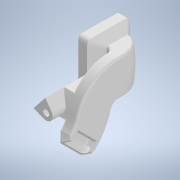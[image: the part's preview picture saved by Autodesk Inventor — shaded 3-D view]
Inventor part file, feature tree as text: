
AUTODESK INVENTOR PART (.ipt)
format: ipt  version: 2022 (Build 260153070, 153G)  size: 797,184 bytes
history: native  units: in
note: dims shown in document units (in); Inventor stores cm internally (conversion verified against a paired STEP export)
features: sketch x21, extrude x14, plane x11, reference x9, other x7, loft x6, fillet x2, sweep x2, projected_geometry x2
ambient origin geometry x8: Origin, YZ Plane, XZ Plane, XY Plane, X Axis, Y Axis, Z Axis, Center Point
bodies: Solid1 (feature_tree)
feature tree (74):
  sketch  "Sketch1"  dims[d0=-0.1969in d1=0.7087in d2=0.0in]
  plane  "Work Plane1"
  extrude  "Extrusion1"  Depth=0.7087in TaperAngle=0.0deg
  plane  "Work Plane2"
  sketch  "Sketch3"  dims[d5=0.1575in d6=-0.1575in]
  plane  "Work Plane3"
  extrude  "Extrusion2"  Depth=0.2441in
  extrude  "Extrusion3"  [1 undecoded]
  plane  "Work Plane4"
  sketch  "Sketch5"  dims[d10=0.0984in d11=0.0in d12=-0.0787in]
  extrude  "Extrusion4"  Depth=0.0906in TaperAngle=0.0deg
  extrude  "Extrusion5"  [1 undecoded]
  extrude  "Extrusion6"  Depth=0.4961in
  fillet  "Fillet1"  Radius=0.7776in
  sketch  "Sketch7"  dims[d16=0.6122in d17=0.0394in]
  plane  "Work Plane5"
  sweep  "Sweep1"
  plane  "Work Plane7"
  sketch  "Sketch10"  dims[d20=0.0394in d21=0.0394in]
  loft  "Loft1"
  loft  "Loft2"
  extrude  "Extrusion8"  Depth=0.0689in
  extrude  "Extrusion9"  Depth=0.0689in
  plane  "Work Plane9"
  sketch  "Sketch15"  dims[d26=0.0689in d27=0.9843in]
  extrude  "Extrusion7"  Depth=0.9843in
  loft  "Loft3"
  loft  "Loft4"
  sketch  "Sketch18"  dims[d28=0.315in d29=0.1969in d30=0.0in]
  plane  "Work Plane12"
  sketch  "Sketch23"  dims[d31=0.0787in d32=0.0in d33=0.0787in]
  sketch  "Sketch24"  dims[d34=0.0787in d35=0.0in d36=0.1969in d37=0.0in]
  extrude  "Extrusion11"  Depth=0.1969in TaperAngle=0.0deg
  loft  "Loft6"
  loft  "Loft7"
  sweep  "Sweep2"
  fillet  "Fillet4"  Radius=0.0394in
  sketch  "Sketch30"  dims[d47=0.0in d49=0.125in d50=0.0in d51=0.0in d52=0.5512in d53=75.0deg d54=0.1772in d56=0.2756in d57=0.5906in d58=0.2405in d71=0.0394in d72=0.0394in d73=0.0394in d74=0.0394in d75=0.0394in d76=0.0394in d77=0.0984in d78=0.5512in d79=0.0197in d80=0.0in d81=90.0deg d82=0.0in d83=90.0deg d84=0.0in d85=90.0deg d86=0.0in d87=90.0deg d90=0.3937in d91=0.0in d92=0.315in d93=0.0787in d94=0.0in d101=0.1181in d102=0.0394in d103=0.0394in d104=0.0394in d106=0.6299in d107=0.315in d108=0.0394in d109=0.0in d110=90.0deg d111=0.0in d112=90.0deg d113=0.0in d114=90.0deg d117=0.0in d118=90.0deg d121=0.2756in d122=90.0deg d123=0.0394in d124=0.0591in d132=90.0deg d133=90.0deg d134=0.0in d135=90.0deg d136=0.0in d137=90.0deg d138=0.0in d139=90.0deg d140=0.0in d141=90.0deg d143=0.0in d144=90.0deg d145=0.0in d146=90.0deg d147=0.0in d148=90.0deg d149=0.0in d150=90.0deg d151=0.0in d152=0.0in d153=0.1875in d154=0.0in d155=0.0276in d156=0.1063in d157=0.7087in d158=0.0in d159=0.1969in d160=0.0in d161=0.0394in d162=0.0in d163=0.7874in d164=0.0in d165=0.0394in d166=0.0in]
  extrude  "Extrusion12"  Depth=0.0394in
  sketch  "Sketch28"  dims[d42=0.0394in d43=0.0394in d44=0.0394in]
  plane  "Work Plane16"
  extrude  "Extrusion13"  Depth=0.125in
  extrude  "Extrusion14"  TaperAngle=0.0deg  [1 undecoded]
  extrude  "Extrusion15"  Depth=0.5512in
  reference  "Reference1"
  sketch  "Sketch2"  dims[d3=0.0906in d4=0.2441in]
  reference  "Reference2"
  reference  "Reference3"
  reference  "Reference4"
  reference  "Reference5"
  reference  "Reference6"
  sketch  "Sketch4"  dims[d7=0.2165in d8=0.0906in d9=0.0in]
  reference  "Reference7"
  sketch  "Sketch6"  dims[d13=0.689in d14=0.4961in d15=0.7776in]
  sketch  "Sketch8"  dims[d18=0.0394in d19=0.0394in]
  plane  "Work Plane6"
  other  "Edges1"
  other  "Edges2"
  sketch  "Sketch11"  dims[d22=0.0394in d23=0.0689in]
  sketch  "Sketch12"  dims[d24=0.0689in d25=0.0689in]
  other  "Edges3"
  projected_geometry  "Projected Loop2"
  plane  "Work Plane10"
  projected_geometry  "Projected Loop4"
  sketch  "3D Sketch1"
  sketch  "Sketch25"  dims[d38=0.0394in d39=0.5512in]
  sketch  "Sketch26"  dims[d40=0.1181in d41=0.2461in]
  reference  "Reference9"
  sketch  "Sketch29"  dims[d45=0.0394in d46=0.0394in]
  reference  "Reference10"
  other  "<userpath> laptop\Desktop\Another3dPrinterShroud\MODELS\ENDER 3 ASSEMBLY.iam"
  other  "ENDER 3 ASSEMBLY.iam"
  other  "FRONTPLATE:1"
  other  "ENDER 3 NOZZLE:1"
note: 3 required parameter values undecoded (feature->parameter linkage not recoverable at this tier; creation-order binding heuristic only, values carry confidence <= 0.55)
